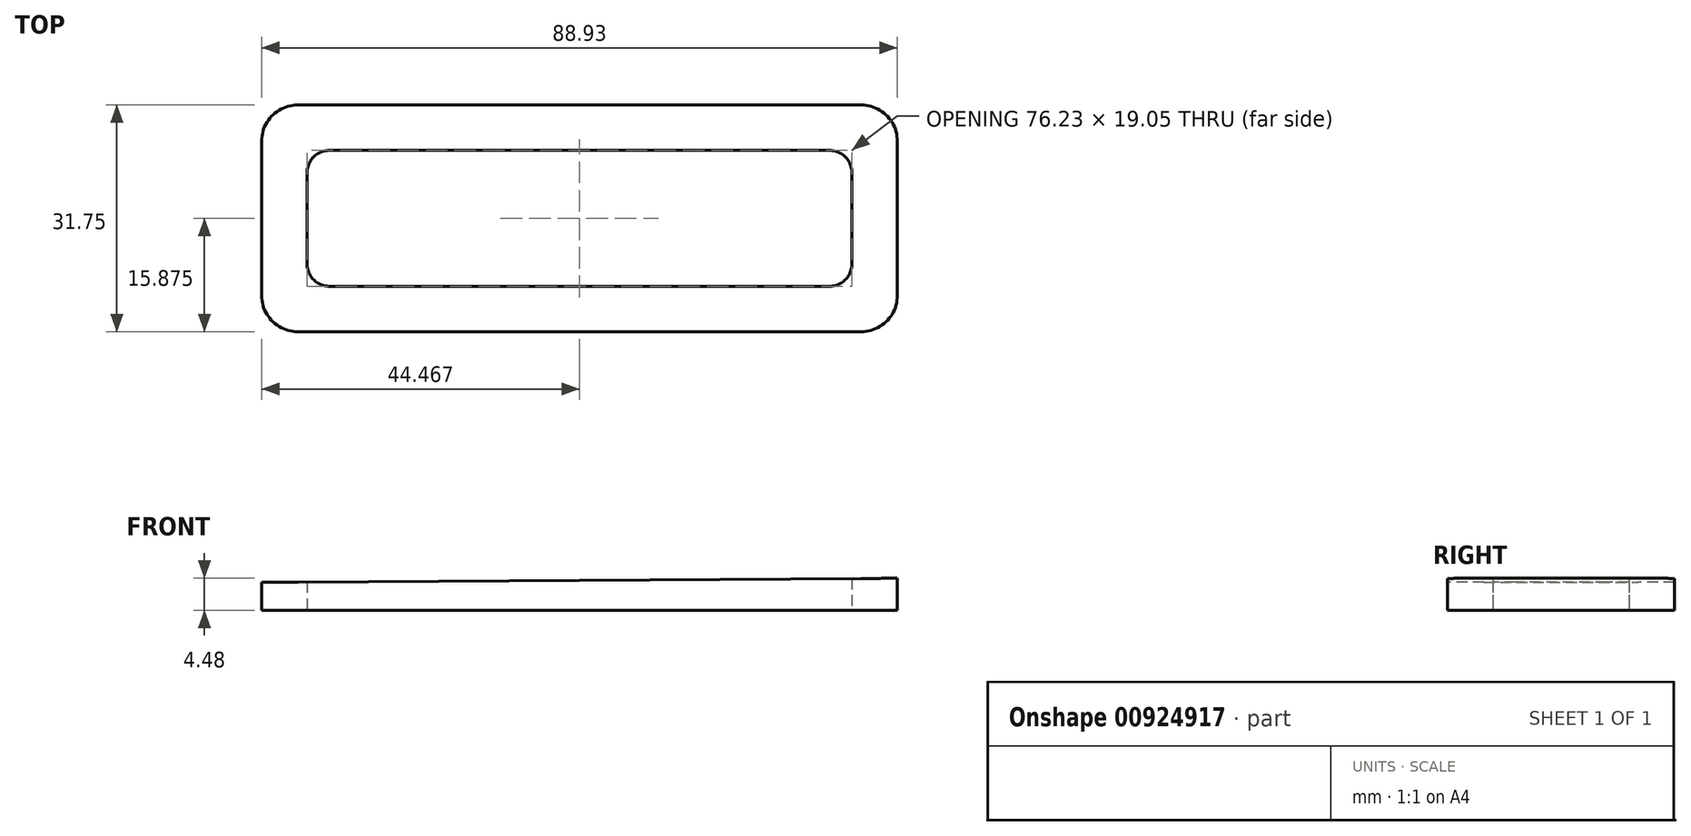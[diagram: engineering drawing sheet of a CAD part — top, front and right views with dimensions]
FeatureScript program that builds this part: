
annotation { "Feature Type Name" : "Feature", "Feature Type Description" : "" }
export const myFeature = defineFeature(function(context is Context, id is Id, definition is map)
    precondition{}
    {
        {
            var Q0;
            Q0=qCreatedBy(makeId("Front.planeOp"),FACE);
            var sketch = newSketch(context, id + "F0", { "sketchPlane" : qUnion([Q0])});
            skLineSegment(sketch, "E0", {"start": v(0, 0) * mm, "end": v(0, 1.59) * mm});
            skLineSegment(sketch, "E1", {"start": v(0, 1.59) * mm, "end": v(609.6, 5.56) * mm});
            skLineSegment(sketch, "E2", {"start": v(609.6, 5.56) * mm, "end": v(609.6, 0) * mm});
            skLineSegment(sketch, "E3", {"start": v(609.6, 0) * mm, "end": v(0, 0) * mm});
            skSolve(sketch);
        }
        {
            var Q0;
            Q0=qCreatedBy(makeId("Front.planeOp"),FACE);
            var sketch = newSketch(context, id + "F1", { "sketchPlane" : qUnion([Q0])});
            skLineSegment(sketch, "E4", {"start": v(609.6, 5.56) * mm, "end": v(520.7, 4.98) * mm});
            skLineSegment(sketch, "E5", {"start": v(520.7, 4.98) * mm, "end": v(520.7, 0) * mm});
            skLineSegment(sketch, "E6", {"start": v(520.7, 0) * mm, "end": v(609.6, 0) * mm});
            skLineSegment(sketch, "E7", {"start": v(609.6, 0) * mm, "end": v(609.6, 5.56) * mm});
            skSolve(sketch);
        }
        {
            var Q0;
            Q0=qCreatedBy(makeId("Front.planeOp"),FACE);
            var sketch = newSketch(context, id + "F2", { "sketchPlane" : qUnion([Q0])});
            skLineSegment(sketch, "E8", {"start": v(444.5, 4.48) * mm, "end": v(444.5, 0) * mm});
            skLineSegment(sketch, "E9", {"start": v(444.5, 0) * mm, "end": v(355.6, 0) * mm});
            skLineSegment(sketch, "E10", {"start": v(-243.84, 0) * mm, "end": v(-243.84, 0) * mm});
            skLineSegment(sketch, "E11", {"start": v(355.57, 3.9) * mm, "end": v(444.5, 4.48) * mm});
            skLineSegment(sketch, "E12", {"start": v(355.57, 3.9) * mm, "end": v(355.6, 0) * mm});
            skSolve(sketch);
        }
        {
            var Q0;
            Q0 = qSketchRegion(id + "F2", true);
            extrude(context, id + "F3", {"entities" : qUnion([Q0]), "depth" : 31.75 * mm, "offsetDistance" : 25.4 * mm});
        }
        {
            var Q0;
            Q0=makeQuery(id+"F3.opExtrude","SWEPT_FACE",FACE,{"disambiguationData":[OSD([sQuery(id+"F2.wireOp",EDGE,"E9")])]});
            var sketch = newSketch(context, id + "F4", { "sketchPlane" : qUnion([Q0])});
            skLineSegment(sketch, "E13.bottom", {"start": v(365.1, 25.4) * mm, "end": v(434.98, 25.4) * mm});
            skLineSegment(sketch, "E13.top", {"start": v(365.1, 6.35) * mm, "end": v(434.98, 6.35) * mm});
            skLineSegment(sketch, "E13.left", {"start": v(361.92, 22.22) * mm, "end": v(361.92, 9.53) * mm});
            skLineSegment(sketch, "E13.right", {"start": v(438.15, 22.23) * mm, "end": v(438.15, 9.53) * mm});
            skPoint(sketch, "E14.visualSharp", {"position": v(361.92, 25.4) * mm});
            skArc(sketch, "E14.filletArc", {"start": v(365.1, 25.4) * mm, "mid": v(362.85, 24.47) * mm, "end": v(361.92, 22.22) * mm});
            skPoint(sketch, "E15.visualSharp", {"position": v(438.15, 25.4) * mm});
            skArc(sketch, "E15.filletArc", {"start": v(438.15, 22.23) * mm, "mid": v(437.22, 24.47) * mm, "end": v(434.98, 25.4) * mm});
            skPoint(sketch, "E16.visualSharp", {"position": v(438.15, 6.35) * mm});
            skArc(sketch, "E16.filletArc", {"start": v(434.98, 6.35) * mm, "mid": v(437.22, 7.28) * mm, "end": v(438.15, 9.53) * mm});
            skPoint(sketch, "E17.visualSharp", {"position": v(361.92, 6.35) * mm});
            skArc(sketch, "E17.filletArc", {"start": v(361.92, 9.52) * mm, "mid": v(362.85, 7.28) * mm, "end": v(365.1, 6.35) * mm});
            skSolve(sketch);
        }
        {
            var Q0;
            Q0=makeQuery(id+"F4.imprint","IMPRINT",FACE,{"disambiguationData":[TD([[makeQuery(id+"F4.imprint","IMPRINT",EDGE,{"derivedFrom":sQuery(id+"F4.wireOp",EDGE,"E13.bottom")}),-1.0]])]});
            extrude(context, id + "F5", {"entities" : qUnion([Q0]), "operationType" : NewBodyOperationType.REMOVE, "endBound" : BoundingType.THROUGH_ALL, "oppositeDirection" : true, "depth" : 25.4 * mm, "offsetDistance" : 25.4 * mm});
        }
        {
            var Q0;
            Q0=makeQuery(id+"F3.opExtrude","CAP_EDGE",EDGE,{"disambiguationData":[OSD([sQuery(id+"F2.wireOp",EDGE,"E8")])],"isStart":false});
            var Q1;
            Q1=makeQuery(id+"F3.opExtrude","CAP_EDGE",EDGE,{"disambiguationData":[OSD([sQuery(id+"F2.wireOp",EDGE,"E12")])],"isStart":false});
            var Q2;
            Q2=makeQuery(id+"F3.opExtrude","CAP_EDGE",EDGE,{"disambiguationData":[OSD([sQuery(id+"F2.wireOp",EDGE,"E12")])],"isStart":true});
            var Q3;
            Q3=makeQuery(id+"F3.opExtrude","CAP_EDGE",EDGE,{"disambiguationData":[OSD([sQuery(id+"F2.wireOp",EDGE,"E8")])],"isStart":true});
            fillet(context, id + "F6", {"entities" : qUnion([Q0, Q1, Q2, Q3]), "radius" : 5.08 * mm, "tangentPropagation" : true, "allowEdgeOverflow" : false});
        }
    });
